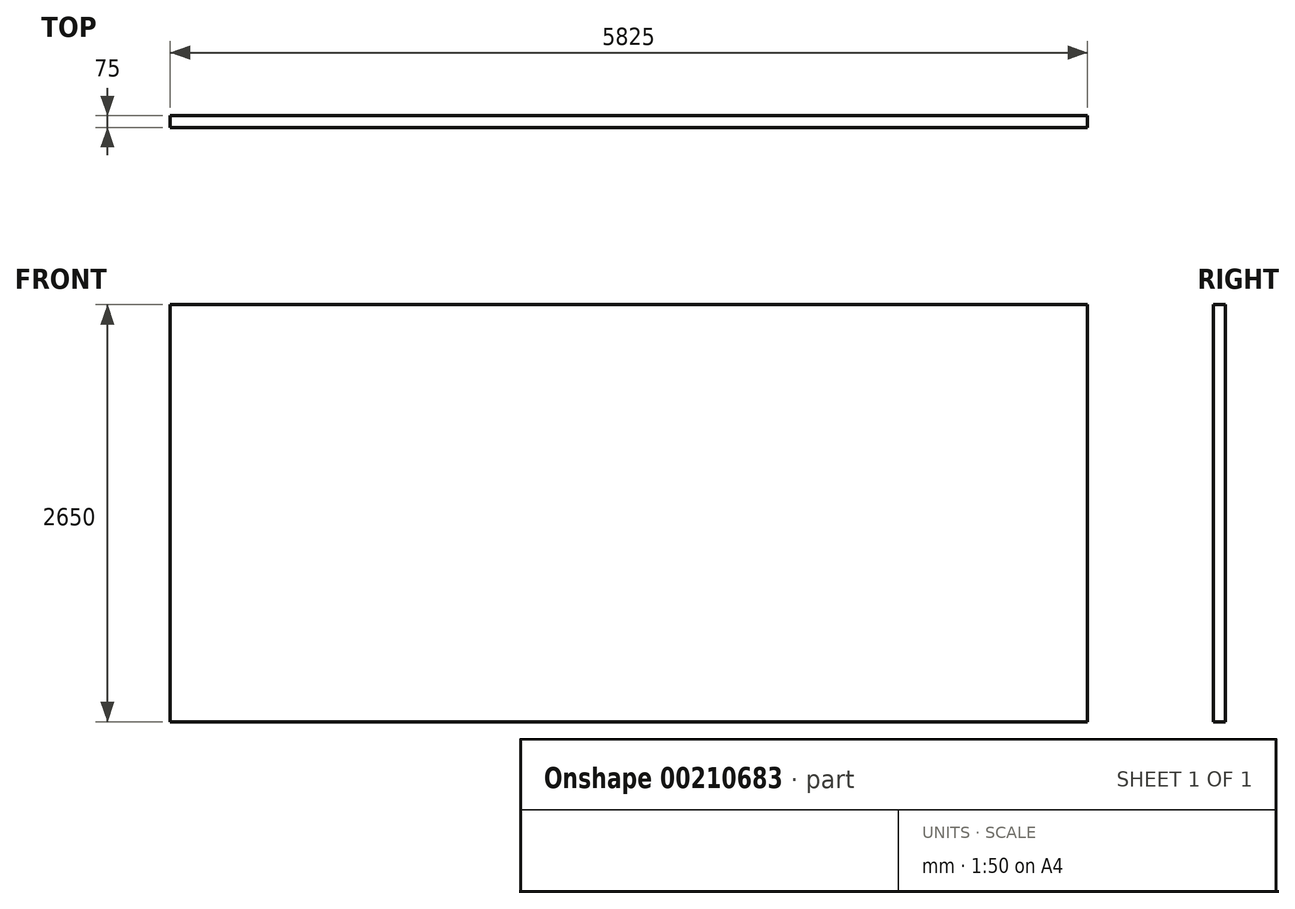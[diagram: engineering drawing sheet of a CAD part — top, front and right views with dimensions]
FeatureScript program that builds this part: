
annotation { "Feature Type Name" : "Feature", "Feature Type Description" : "" }
export const myFeature = defineFeature(function(context is Context, id is Id, definition is map)
    precondition{}
    {
        {
            var Q0;
            Q0=qCreatedBy(makeId("Front.planeOp"),FACE);
            var sketch = newSketch(context, id + "F0", { "sketchPlane" : qUnion([Q0])});
            skLineSegment(sketch, "E0.bottom", {"start": v(0, 0) * mm, "end": v(5825, 0) * mm});
            skLineSegment(sketch, "E0.left", {"start": v(0, 0) * mm, "end": v(0, 2650) * mm});
            skLineSegment(sketch, "E0.right", {"start": v(5825, 0) * mm, "end": v(5825, 2650) * mm});
            skLineSegment(sketch, "E1", {"start": v(0, 2650) * mm, "end": v(5825, 2650) * mm});
            skSolve(sketch);
        }
        {
            var Q0;
            Q0=makeQuery(id+"F0.imprint","IMPRINT",FACE,{"disambiguationData":[TD([[makeQuery(id+"F0.imprint","IMPRINT",EDGE,{"derivedFrom":sQuery(id+"F0.wireOp",EDGE,"E0.bottom")}),1.0]])]});
            extrude(context, id + "F1", {"entities" : qUnion([Q0]), "depth" : 75 * mm});
        }
    });
